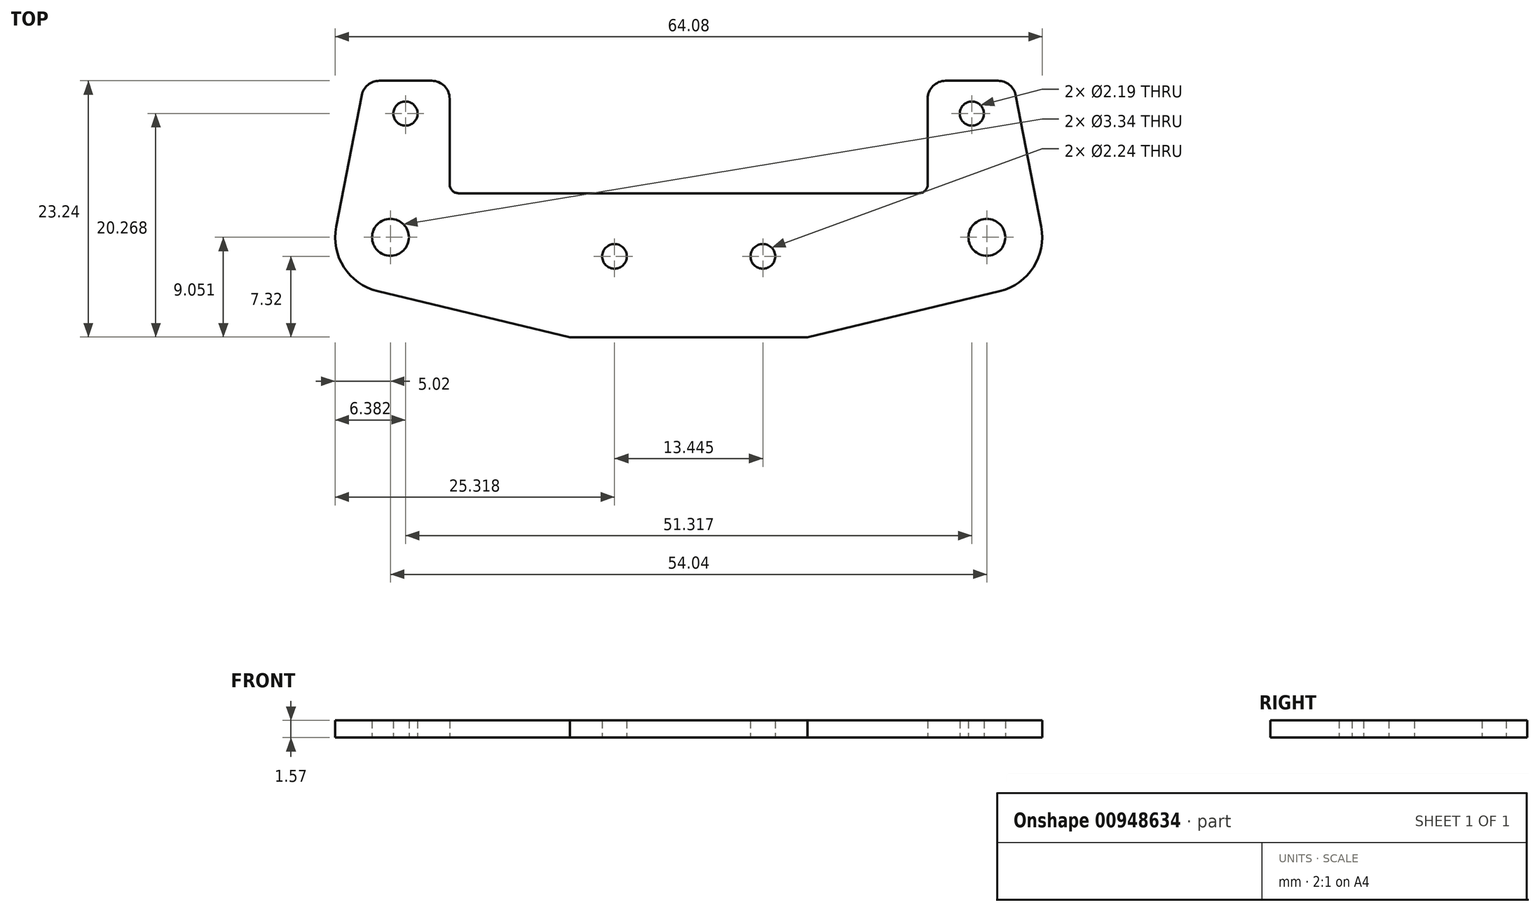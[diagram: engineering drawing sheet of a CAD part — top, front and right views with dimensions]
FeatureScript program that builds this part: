
annotation { "Feature Type Name" : "Feature", "Feature Type Description" : "" }
export const myFeature = defineFeature(function(context is Context, id is Id, definition is map)
    precondition{}
    {
        {
            var Q0;
            Q0=qCreatedBy(makeId("Top.planeOp"),FACE);
            var sketch = newSketch(context, id + "F0", { "sketchPlane" : qUnion([Q0])});
            skLineSegment(sketch, "E0", {"start": v(-25.66, 11.62) * mm, "end": v(-23.29, 11.62) * mm});
            skArc(sketch, "E1", {"start": v(-23.29, 11.62) * mm, "mid": v(-22.14, 11.15) * mm, "end": v(-21.66, 10) * mm});
            skLineSegment(sketch, "E2", {"start": v(-21.66, 10) * mm, "end": v(-21.66, 2.24) * mm});
            skArc(sketch, "E3", {"start": v(-21.66, 2.24) * mm, "mid": v(-21.42, 1.66) * mm, "end": v(-20.85, 1.42) * mm});
            skLineSegment(sketch, "E4", {"start": v(-20.85, 1.42) * mm, "end": v(0, 1.42) * mm});
            skCircle(sketch, "E5", {"center": v(-27.02, -2.57) * mm, "radius": 1.67 * mm});
            skCircle(sketch, "E6", {"center": v(-25.66, 8.65) * mm, "radius": 1.1 * mm});
            skCircle(sketch, "E7", {"center": v(-6.72, -4.3) * mm, "radius": 1.12 * mm});
            skArc(sketch, "E8", {"start": v(-31.94, -1.61) * mm, "mid": v(-31.24, -5.28) * mm, "end": v(-28.19, -7.45) * mm});
            skLineSegment(sketch, "E9", {"start": v(-28.19, -7.45) * mm, "end": v(-10.77, -11.62) * mm});
            skLineSegment(sketch, "E10", {"start": v(-31.94, -1.61) * mm, "end": v(-29.63, 10.3) * mm});
            skArc(sketch, "E11", {"start": v(-29.63, 10.3) * mm, "mid": v(-29.06, 11.25) * mm, "end": v(-28.03, 11.62) * mm});
            skLineSegment(sketch, "E12", {"start": v(-28.03, 11.62) * mm, "end": v(-25.66, 11.62) * mm});
            skLineSegment(sketch, "E13", {"start": v(-10.77, -11.62) * mm, "end": v(0, -11.62) * mm});
            skLineSegment(sketch, "E14", {"start": v(25.66, 11.62) * mm, "end": v(23.29, 11.62) * mm});
            skArc(sketch, "E15", {"start": v(23.29, 11.62) * mm, "mid": v(22.14, 11.15) * mm, "end": v(21.66, 10) * mm});
            skLineSegment(sketch, "E16", {"start": v(21.66, 10) * mm, "end": v(21.66, 2.24) * mm});
            skArc(sketch, "E17", {"start": v(21.66, 2.24) * mm, "mid": v(21.42, 1.66) * mm, "end": v(20.85, 1.42) * mm});
            skLineSegment(sketch, "E18", {"start": v(20.85, 1.42) * mm, "end": v(0, 1.42) * mm});
            skCircle(sketch, "E19", {"center": v(27.02, -2.57) * mm, "radius": 1.67 * mm});
            skCircle(sketch, "E20", {"center": v(25.66, 8.65) * mm, "radius": 1.1 * mm});
            skCircle(sketch, "E21", {"center": v(6.72, -4.3) * mm, "radius": 1.12 * mm});
            skArc(sketch, "E22", {"start": v(28.19, -7.45) * mm, "mid": v(31.24, -5.28) * mm, "end": v(31.94, -1.61) * mm});
            skLineSegment(sketch, "E23", {"start": v(28.19, -7.45) * mm, "end": v(10.77, -11.62) * mm});
            skLineSegment(sketch, "E24", {"start": v(31.94, -1.61) * mm, "end": v(29.63, 10.3) * mm});
            skArc(sketch, "E25", {"start": v(29.63, 10.3) * mm, "mid": v(29.06, 11.25) * mm, "end": v(28.03, 11.62) * mm});
            skLineSegment(sketch, "E26", {"start": v(28.03, 11.62) * mm, "end": v(25.66, 11.62) * mm});
            skLineSegment(sketch, "E27", {"start": v(10.77, -11.62) * mm, "end": v(0, -11.62) * mm});
            skSolve(sketch);
        }
        {
            var Q0;
            Q0=makeQuery(id+"F0.imprint","IMPRINT",FACE,{"disambiguationData":[TD([[makeQuery(id+"F0.imprint","IMPRINT",EDGE,{"derivedFrom":sQuery(id+"F0.wireOp",EDGE,"E0")}),-1.0]])]});
            extrude(context, id + "F1", {"entities" : qUnion([Q0]), "depth" : 1.57 * mm, "offsetDistance" : 25.4 * mm});
        }
    });
